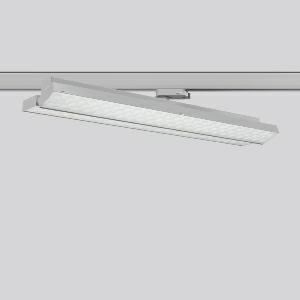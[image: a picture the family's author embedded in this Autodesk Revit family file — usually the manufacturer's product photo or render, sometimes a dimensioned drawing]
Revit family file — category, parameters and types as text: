
# Revit family: tx-move_742163_004_76_3d52
name_source: partatom
category: Lighting Fixtures
units: mm (PartAtom-declared; Revit-internal decimal feet)

## family parameters
Cut with Voids When Loaded = No
Host = Face
Light Source = No
Part Type = Normal
Room Calculation Point = No
Round Connector Dimension = Use Diameter
Shared = No

## types (1)
- MultiLumen 1 (1 x LED Modul 830, 2750 lm, 3000)
    Apparent Load = 41 VA
    CIE Flux Codes = 65 90 98 100 100
    Color Rendering = 80
    Color Temperature = 3000
    Default Elevation = 1800 mm
    Description = Series: TX-MOVE
Multifunctional surface-mounted spotlight for area lighting. Very flat design. Housing: sheet steel, powder-coated. Rotation range: 356°. Swivel range: 90°. Consistent alignment possible with visible tilt scale. High-efficiency LED units with optimum light control thanks to clear plastic (PC) lens optics. Spezielle Mikrostrukturen reduzieren Gelbsaum. Asymmetrical light distribution. With adapter for RZB 3-circuit DALI tracks. Suitable for Track on ceiling. MultiLumen: Luminous flux adjustable in 3 steps. Factory setting is the highest luminous flux. Environmentally friendly and resource-saving due to replaceable and recyclable components. 
Colour: silver, matt (approx. RAL 9006)
Length: 570 mm
Width: 119 mm
Height: 88 mm
Lamp: LED
Socket: without socket
Colour temperature: 3000K
Colour rendering index (CRI): 80
System power: 41 W
Rated luminous flux: 5500 lm
Luminous efficiency: 134 lm/W
System power 2: 57 W
Rated luminous flux 2: 7400 lm
Luminous efficiency 2: 130 lm/W
System power 3: 73 W
Rated luminous flux 3: 9050 lm
Luminous efficiency 3: 124 lm/W
Control gear: Dimmable EVG, DALI
Protection class: I
Type of protection: IP 20
    Height = 75 mm
    Lamp = 1 x LED Modul 830
    Lamp Light Flux = 2750 lm
    Lamp count = 1
    Length = 569 mm
    Lifetime = 50000 h
    Luminous efficacy = 134 lm/W
    Manufacturer = RZB
    ModVariant = No
    Model = 742163.004.76
    Mounting Place = Ceiling
    Mounting Type = Surface mounted
    Number of Poles = 1
    OnlyDefault = Yes
    Power Factor = 1
    Product Name = TX-MOVE
    Product group = Track mounted projectors
    ProductGroupID = 301
    Protection Class = Protection class I
    Protection Degree = IP 20
    RLX_Detail_Level = 1
    RLX_Emergency_Light_Flux = 0 lm
    RLX_Emergency_Type = 0
    RLX_Emergency_Type_DB = No
    RlxData = <blob elided: 53745 chars, md5=90cf1ab4>
    Socket = socket
    Standby Power = 0 W
    System Light Flux = 5500 lm
    System Power = 41 W
    Type Comments = MultiLumen 1
    Type Image = 742162.004.jpg
    URL = http://relux.com
    VarID = multilumen_1
    Voltage = 0 V
    Weight = 0.00 kg
    Width = 119 mm

## geometry (parser evidence)
native form markers: Blend x4, Sweep x17
no freeform markers — native parametric forms only
